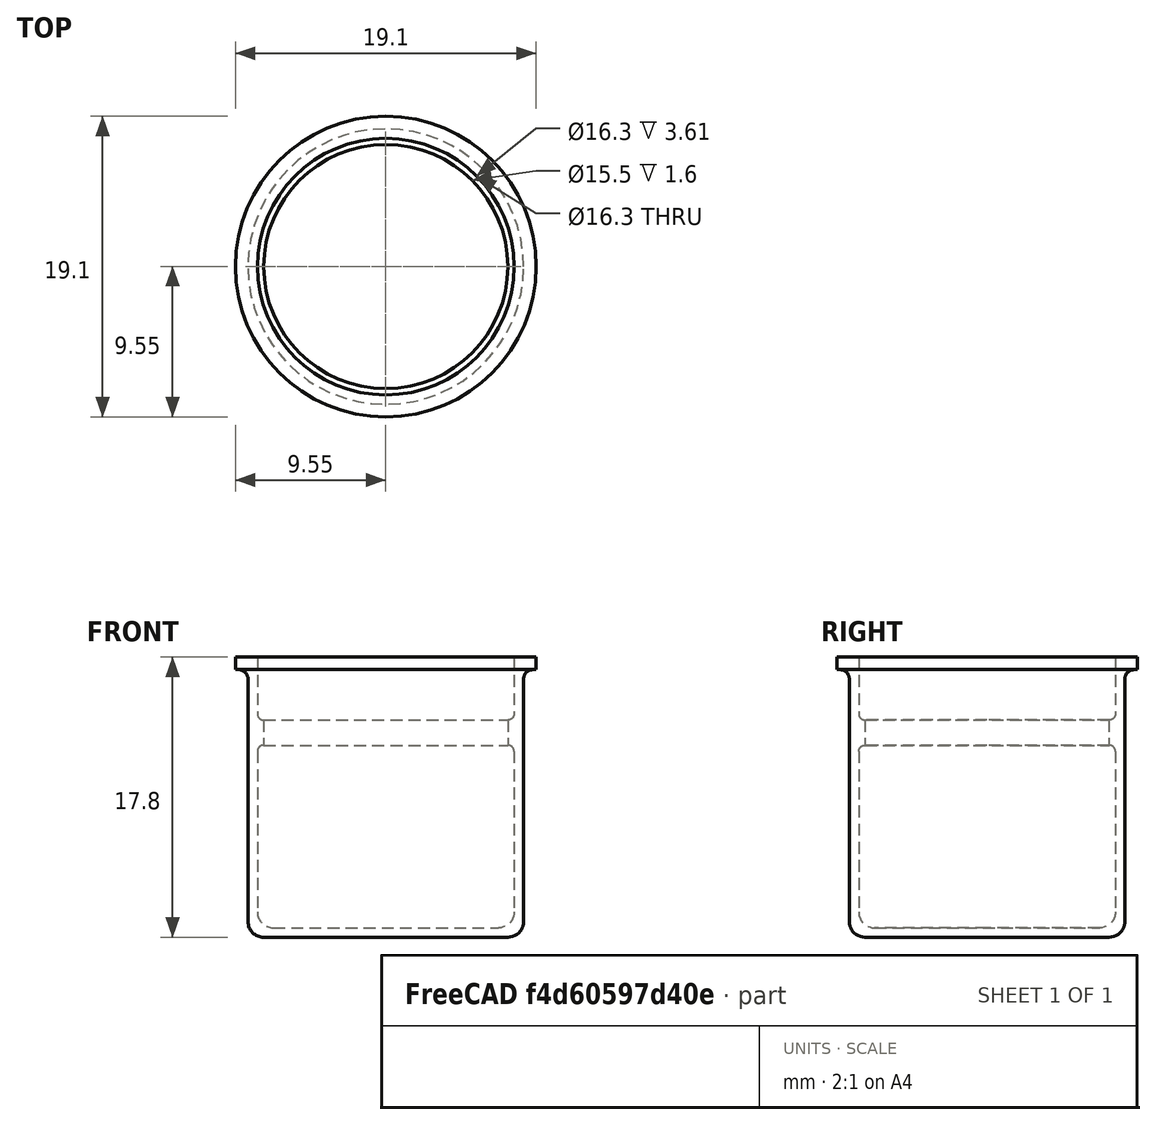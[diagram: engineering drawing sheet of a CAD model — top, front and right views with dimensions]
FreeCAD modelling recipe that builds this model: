
FCSTD DOCUMENT  (FreeCAD 1.0R39109 (Git))
Label: Model
License: All rights reserved
LicenseURL: https://en.wikipedia.org/wiki/All_rights_reserved
objects: Sketcher::SketchObject×1, PartDesign::Revolution×1, PartDesign::Body×1
note: 6 computed .brp shape members not serialized (recipe doc carries the construction recipe); baked Part::Feature solids carry a one-line shape summary decoded from their .brp

FEATURE [Sketcher::SketchObject] Sketch
  ArcFitTolerance = 1e-06
  AttachmentSupport = -> [XZ_Plane]
  FullyConstrained = true
  MakeInternals = false
  MapMode = 5
  Placement = pos=(0,0,0) rot=(1,0,0;1.5708rad)
  expr: Constraints[27] = 17
  sketch-geometry (22):
    g0: LineSegment StartX=0 StartY=0 StartZ=0 EndX=-7.75 EndY=0 EndZ=0
    g1: LineSegment StartX=-8.75 StartY=1 StartZ=0 EndX=-8.75 EndY=16.4 EndZ=0
    g2: LineSegment StartX=-9.35 StartY=17 StartZ=0 EndX=-9.55 EndY=17 EndZ=0
    g3: LineSegment StartX=-9.55 StartY=17 StartZ=0 EndX=-9.55 EndY=17.8 EndZ=0
    g4: LineSegment StartX=-9.55 StartY=17.8 StartZ=0 EndX=-8.15 EndY=17.8 EndZ=0
    g5: LineSegment StartX=-8.15 StartY=17.8 StartZ=0 EndX=-8.15 EndY=14.19 EndZ=0
    g6: LineSegment StartX=-7.76 StartY=13.8 StartZ=0 EndX=-7.75 EndY=13.8 EndZ=0
    g7: LineSegment StartX=-7.75 StartY=13.8 StartZ=0 EndX=-7.75 EndY=12.2 EndZ=0
    g8: LineSegment StartX=-7.75 StartY=12.2 StartZ=0 EndX=-7.76 EndY=12.2 EndZ=0
    g9: LineSegment StartX=-8.15 StartY=11.81 StartZ=0 EndX=-8.15 EndY=1.6 EndZ=0
    g10: LineSegment StartX=-7.15 StartY=0.6 StartZ=0 EndX=0 EndY=0.6 EndZ=0
    g11: LineSegment StartX=0 StartY=0.6 StartZ=0 EndX=0 EndY=0 EndZ=0
    g12: ArcOfCircle CenterX=-7.15 CenterY=1.6 CenterZ=0 NormalX=0 NormalY=0 NormalZ=1 AngleXU=0 Radius=1 StartAngle=3.14159 EndAngle=4.71239
    g13: GeomPoint [constr] X=-8.15 Y=0.6 Z=0
    g14: ArcOfCircle CenterX=-7.75 CenterY=1 CenterZ=0 NormalX=0 NormalY=0 NormalZ=1 AngleXU=0 Radius=1 StartAngle=3.14159 EndAngle=4.71239
    g15: GeomPoint [constr] X=-8.75 Y=0 Z=0
    g16: ArcOfCircle CenterX=-7.76 CenterY=14.19 CenterZ=0 NormalX=0 NormalY=0 NormalZ=1 AngleXU=0 Radius=0.39 StartAngle=3.14159 EndAngle=4.71239
    g17: GeomPoint [constr] X=-8.15 Y=13.8 Z=0
    g18: ArcOfCircle CenterX=-7.76 CenterY=11.81 CenterZ=0 NormalX=0 NormalY=0 NormalZ=1 AngleXU=0 Radius=0.39 StartAngle=1.5708 EndAngle=3.14159
    g19: GeomPoint [constr] X=-8.15 Y=12.2 Z=0
    g20: ArcOfCircle CenterX=-9.35 CenterY=16.4 CenterZ=0 NormalX=0 NormalY=0 NormalZ=1 AngleXU=0 Radius=0.6 StartAngle=1e-16 EndAngle=1.5708
    g21: GeomPoint [constr] X=-8.75 Y=17 Z=0
  constraints (55):
    c: Coincident(g-1,g0)
    c: PointOnObject(g15,g-1)
    c: Vertical(g1)
    c: Coincident(g2,g3)
    c: Coincident(g3,g4)
    c: Coincident(g4,g5)
    c: Vertical(g5)
    c: Coincident(g6,g7)
    c: Vertical(g7)
    c: Coincident(g7,g8)
    c: Vertical(g9)
    c: Horizontal(g10)
    c: Coincident(g11,g10)
    c: Coincident(g11,g0)
    c: Vertical(g11)
    c: DistanceX(g15,g0) = 8.75
    c: DistanceX(g2,g21) = 0.8
    c: Vertical(g3)
    c: Horizontal(g2)
    c: Horizontal(g4)
    c: Horizontal(g6)
    c: Horizontal(g8)
    c: DistanceY(g3,g3) = 0.8
    c: Distance(g4,g4) = 1.4
    c: DistanceY(g17,g5) = 4
    c: Distance(g17,g6) = 0.4
    c: DistanceY(g7,g7) = 1.6
    c: DistanceY(g15,g21) = 17
    c: DistanceY(g11,g11) = 0.6
    c: PointOnObject(g13,g10)
    c: PointOnObject(g13,g9)
    c: Tangent(g10,g12) = -1.5708
    c: Tangent(g9,g12) = -1.5708
    c: PointOnObject(g15,g0)
    c: PointOnObject(g15,g1)
    c: Tangent(g0,g14) = 1.5708
    c: Tangent(g1,g14) = 1.5708
    c: Equal(g14,g12)
    c: Radius(g14) = 1
    c: PointOnObject(g17,g5)
    c: PointOnObject(g17,g6)
    c: Tangent(g5,g16) = -1.5708
    c: Tangent(g6,g16) = -1.5708
    c: PointOnObject(g19,g9)
    c: PointOnObject(g19,g8)
    c: Tangent(g9,g18) = -1.5708
    c: Tangent(g8,g18) = -1.5708
    c: PointOnObject(g21,g2)
    c: PointOnObject(g21,g1)
    c: Tangent(g2,g20) = -1.5708
    c: Tangent(g1,g20) = -1.5708
    c: Radius(g20) = 0.6
    c: Radius(g16) = 0.39
    c: Equal(g16,g18)
    c: Equal(g6,g8)
FEATURE [PartDesign::Revolution] Revolution
  Angle = 360
  Angle2 = 60
  Axis = (0,2e-16,1)
  Base = (0,0,0)
  Placement = pos=(0,0,0) rot=(1,0,0;1.5708rad)
  Profile = -> Sketch
  ReferenceAxis = -> Sketch [V_Axis]
  Refine = true
  Suppressed = false
  Type = 0
FEATURE [PartDesign::Body] Body
  AllowCompound = false
  Group = -> [Sketch,Revolution]
  Origin = -> Origin
  Tip = -> Revolution
